# Revit family: РИДАН_Клапан термостатический TR_G New
name_source: partatom
category: Арматура трубопроводов
units: mm (PartAtom-declared; Revit-internal decimal feet)

## family parameters
Всегда вертикально = Да
На основе рабочей плоскости = Нет
Общий = Нет
При загрузке вырезать с полостями = Нет
Размер круглого соединителя = Использовать диаметр
Тип детали = Вставляется

## types (8) — shared parameters
ADSK_Версия Revit = 2019
ADSK_Версия семейства = 1.0
ADSK_Единица измерения = шт.
ADSK_Завод-изготовитель = ООО «Ридан-Трейд»
ADSK_Количество = 1
ADSK_Потеря давления жидкости = 0.0 Па
ADSK_Расход жидкости = 0.0 л/с
LT = TR-G
e = 26 мм
f = 21 мм
i = 36 мм
zero-valued in all types: ADSK_Масса

## per-type parameters (varying)
| type | ADSK_Диаметр условный | ADSK_Код изделия | ADSK_Марка | ADSK_Наименование | ADSK_Пропускная способность | a | b | c | d | d1 | g | g1 | h | j | k | l | m | n | Термоголовка |
| Ду15+TR70 | 15 мм | 013G9024R | TR-G DN15 | Клапан терморегулятора с повышенной пропускной способностью TR-G PN16, Tmax=120C, DN15 | 0.3 л/с | 10 мм | 54 мм | 10 мм | 21 мм | 10 мм | 25 мм | 24 мм | 21 мм | 27 мм | 30 мм | 13 мм | 21 мм | 75 мм | Влж_РИДАН_TR70_Термостатический элемент : TR 70 |
| Ду20+TR70 | 20 мм | 013G9026R | TR-G DN20 | Клапан терморегулятора с повышенной пропускной способностью TR-G PN16, Tmax=120C, DN20 | 0.4 л/с | 13 мм | 56 мм | 14 мм | 23 мм | 11 мм | 32 мм | 31 мм | 26 мм | 31 мм | 37 мм | 15 мм | 26 мм | 81 мм | Влж_РИДАН_TR70_Термостатический элемент : TR 70 |
| Ду15+TR8000 | 15 мм | 013G9024R | TR-G DN15 | Клапан терморегулятора с повышенной пропускной способностью TR-G PN16, Tmax=120C, DN15 | 0.3 л/с | 10 мм | 54 мм | 10 мм | 21 мм | 10 мм | 25 мм | 24 мм | 21 мм | 27 мм | 30 мм | 13 мм | 21 мм | 75 мм | Влж_РИДАН_Термостатические элементы серии TR 8000 : TR 8000 |
| Ду20+TR8000 | 20 мм | 013G9026R | TR-G DN20 | Клапан терморегулятора с повышенной пропускной способностью TR-G PN16, Tmax=120C, DN20 | 0.4 л/с | 13 мм | 56 мм | 14 мм | 23 мм | 11 мм | 32 мм | 31 мм | 26 мм | 31 мм | 37 мм | 15 мм | 26 мм | 81 мм | Влж_РИДАН_Термостатические элементы серии TR 8000 : TR 8000 |
| Ду15+TR9000 Ultra | 15 мм | 013G9024R | TR-G DN15 | Клапан терморегулятора с повышенной пропускной способностью TR-G PN16, Tmax=120C, DN15 | 0.3 л/с | 10 мм | 54 мм | 10 мм | 21 мм | 10 мм | 25 мм | 24 мм | 21 мм | 27 мм | 30 мм | 13 мм | 21 мм | 75 мм | Влж_РИДАН_Термостатические элементы серии TR 9000 Ultra : TR 9000 Ultra |
| Ду20+TR9000 Ultra | 20 мм | 013G9026R | TR-G DN20 | Клапан терморегулятора с повышенной пропускной способностью TR-G PN16, Tmax=120C, DN20 | 0.4 л/с | 13 мм | 56 мм | 14 мм | 23 мм | 11 мм | 32 мм | 31 мм | 26 мм | 31 мм | 37 мм | 15 мм | 26 мм | 81 мм | Влж_РИДАН_Термостатические элементы серии TR 9000 Ultra : TR 9000 Ultra |
| Ду15+TR9005 Ultra | 15 мм | 013G9024R | TR-G DN15 | Клапан терморегулятора с повышенной пропускной способностью TR-G PN16, Tmax=120C, DN15 | 0.3 л/с | 10 мм | 54 мм | 10 мм | 21 мм | 10 мм | 25 мм | 24 мм | 21 мм | 27 мм | 30 мм | 13 мм | 21 мм | 75 мм | Влж_РИДАН_Термостатические элементы серии TR 9000 Ultra : TR 9005 Ultra |
| Ду20+TR9005 Ultra | 20 мм | 013G9026R | TR-G DN20 | Клапан терморегулятора с повышенной пропускной способностью TR-G PN16, Tmax=120C, DN20 | 0.4 л/с | 13 мм | 56 мм | 14 мм | 23 мм | 11 мм | 32 мм | 31 мм | 26 мм | 31 мм | 37 мм | 15 мм | 26 мм | 81 мм | Влж_РИДАН_Термостатические элементы серии TR 9000 Ultra : TR 9005 Ultra |
